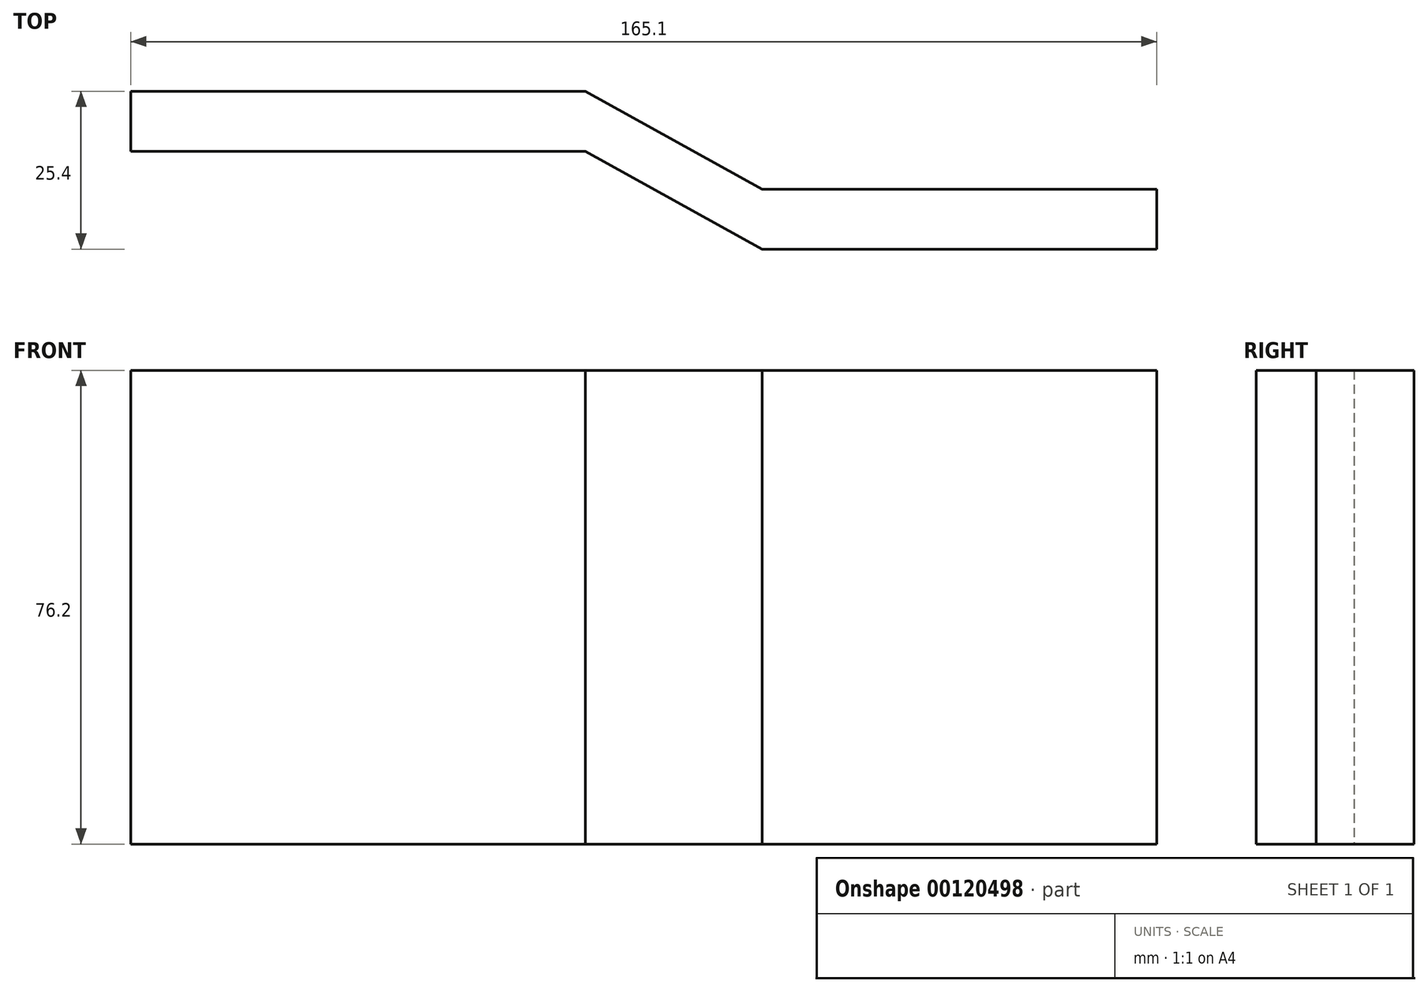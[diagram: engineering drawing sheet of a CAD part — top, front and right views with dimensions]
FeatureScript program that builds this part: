
annotation { "Feature Type Name" : "Feature", "Feature Type Description" : "" }
export const myFeature = defineFeature(function(context is Context, id is Id, definition is map)
    precondition{}
    {
        {
            var Q0;
            Q0=qCreatedBy(makeId("Top.planeOp"),FACE);
            var sketch = newSketch(context, id + "F0", { "sketchPlane" : qUnion([Q0])});
            skLineSegment(sketch, "E0.bottom", {"start": v(-80.3, 10.38) * mm, "end": v(-7.14, 10.38) * mm});
            skLineSegment(sketch, "E0.top", {"start": v(-80.3, 20.04) * mm, "end": v(-7.14, 20.04) * mm});
            skLineSegment(sketch, "E0.left", {"start": v(-80.3, 10.38) * mm, "end": v(-80.3, 20.04) * mm});
            skLineSegment(sketch, "E1.bottom", {"start": v(21.3, 4.29) * mm, "end": v(84.8, 4.29) * mm});
            skLineSegment(sketch, "E1.top", {"start": v(21.3, -5.36) * mm, "end": v(84.8, -5.36) * mm});
            skLineSegment(sketch, "E1.right", {"start": v(84.8, 4.29) * mm, "end": v(84.8, -5.36) * mm});
            skLineSegment(sketch, "E2", {"start": v(-7.14, 20.04) * mm, "end": v(21.3, 4.29) * mm});
            skLineSegment(sketch, "E3", {"start": v(-7.14, 10.38) * mm, "end": v(21.3, -5.36) * mm});
            skSolve(sketch);
        }
        {
            var Q0;
            Q0 = qSketchRegion(id + "F0", true);
            extrude(context, id + "F1", {"entities" : qUnion([Q0]), "depth" : 76.2 * mm});
        }
    });
